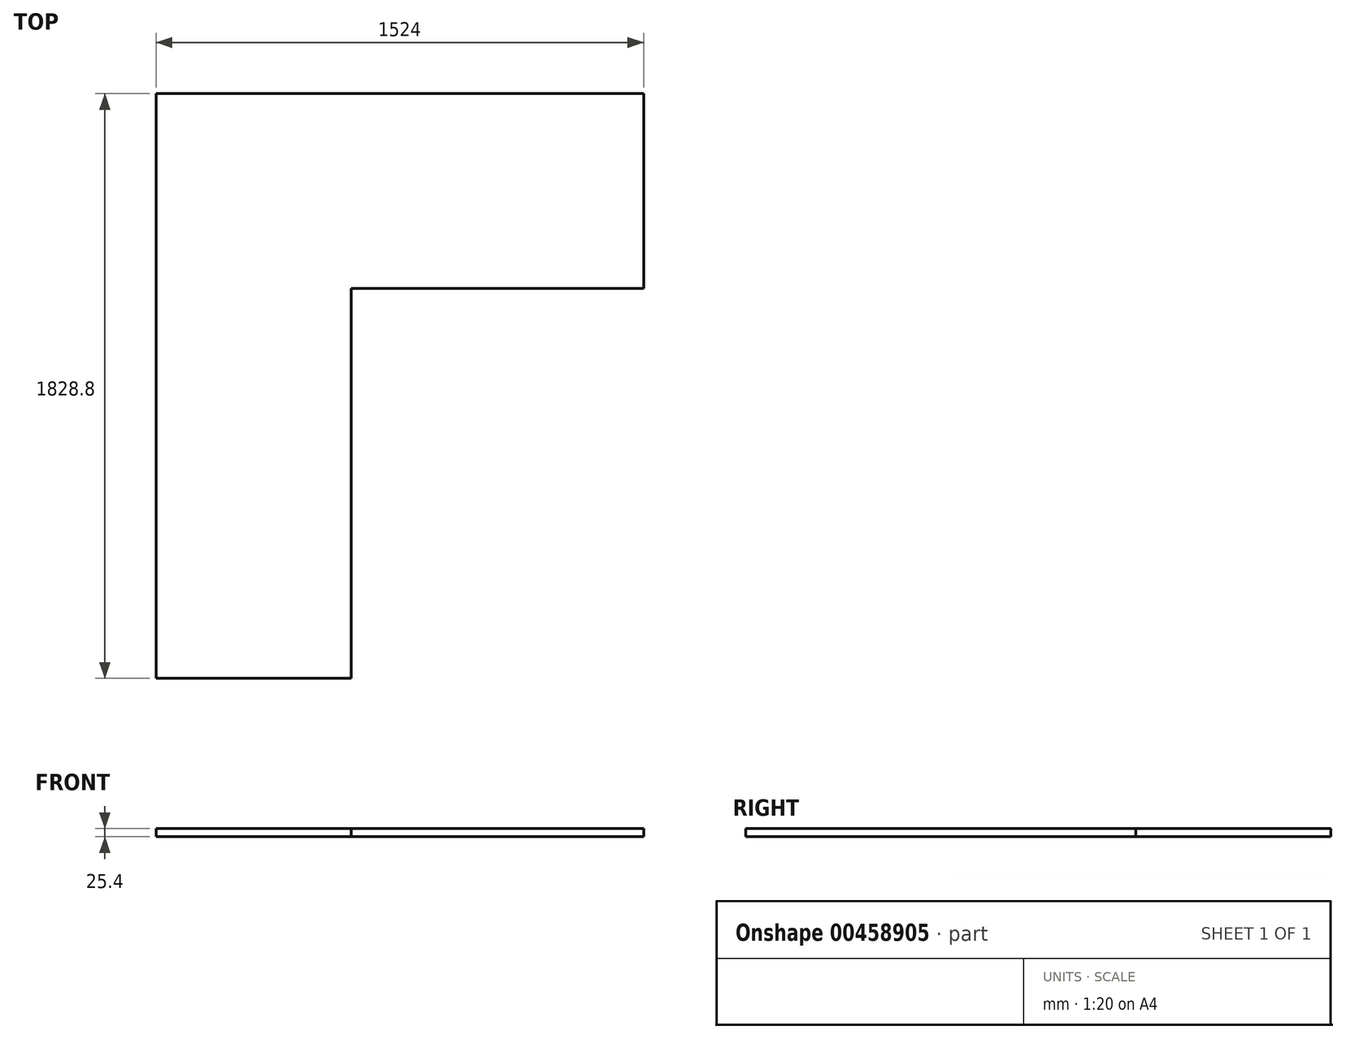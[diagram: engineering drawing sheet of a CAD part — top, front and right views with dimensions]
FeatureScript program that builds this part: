
annotation { "Feature Type Name" : "Feature", "Feature Type Description" : "" }
export const myFeature = defineFeature(function(context is Context, id is Id, definition is map)
    precondition{}
    {
        {
            var Q0;
            Q0=qCreatedBy(makeId("Top.planeOp"),FACE);
            var sketch = newSketch(context, id + "F0", { "sketchPlane" : qUnion([Q0])});
            skLineSegment(sketch, "E0", {"start": v(-452.2, 1303.32) * mm, "end": v(-452.2, -525.48) * mm});
            skLineSegment(sketch, "E1", {"start": v(-452.2, -525.48) * mm, "end": v(157.4, -525.48) * mm});
            skLineSegment(sketch, "E2", {"start": v(157.4, -525.48) * mm, "end": v(157.4, 693.72) * mm});
            skLineSegment(sketch, "E3", {"start": v(157.4, 693.72) * mm, "end": v(1071.8, 693.72) * mm});
            skLineSegment(sketch, "E4", {"start": v(1071.8, 693.72) * mm, "end": v(1071.8, 1303.32) * mm});
            skLineSegment(sketch, "E5", {"start": v(1071.8, 1303.32) * mm, "end": v(-452.2, 1303.32) * mm});
            skSolve(sketch);
        }
        {
            var Q0;
            Q0=makeQuery(id+"F0.imprint","IMPRINT",FACE,{"disambiguationData":[TD([[makeQuery(id+"F0.imprint","IMPRINT",EDGE,{"derivedFrom":sQuery(id+"F0.wireOp",EDGE,"E0")}),1.0]])]});
            extrude(context, id + "F1", {"entities" : qUnion([Q0]), "depth" : 25.4 * mm});
        }
    });
